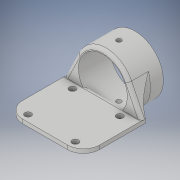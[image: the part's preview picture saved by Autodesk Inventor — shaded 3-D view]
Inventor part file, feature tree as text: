
AUTODESK INVENTOR PART (.ipt)
format: ipt  version: 2018 (Build 220112000, 112)  size: 258,048 bytes
history: native  units: in
note: dims shown in document units (in); Inventor stores cm internally (conversion verified against a paired STEP export)
features: extrude x7, sketch x5, fillet x5, plane x1
ambient origin geometry x8: Origin, YZ Plane, XZ Plane, XY Plane, X Axis, Y Axis, Z Axis, Center Point
bodies: Solid1 (feature_tree)
feature tree (18):
  sketch  "Sketch1"  dims[d0=1.2008in d1=0.0984in]
  extrude  "Extrusion1"  Depth=0.0984in
  plane  "Work Plane1"
  extrude  "Extrusion3"  Depth=1.8898in
  extrude  "Extrusion4"  Depth=0.0984in TaperAngle=0.0deg
  extrude  "Extrusion5"  Depth=1.4173in
  fillet  "Fillet2"  Radius=1.1614in
  extrude  "Extrusion6"  Depth=0.3937in
  fillet  "Fillet3"  Radius=0.1575in
  fillet  "Fillet5"  Radius=0.1575in
  fillet  "Fillet6"  Radius=0.1575in
  fillet  "Fillet7"  Radius=0.0984in
  extrude  "Extrusion7"  Depth=0.3937in TaperAngle=0.0deg
  extrude  "Extrusion8"  Depth=0.3937in
  sketch  "Sketch2"  dims[d2=1.1811in d3=0.0in d8=1.8898in]
  sketch  "Sketch3"  dims[d9=1.5157in d10=0.0984in d11=0.0in]
  sketch  "Sketch4"  dims[d12=1.8898in d13=1.4173in d14=1.1614in]
  sketch  "Sketch5"  dims[d15=1.0906in d16=0.1575in d17=0.1575in d18=0.1575in d19=0.1575in d20=0.0984in d21=0.0in d23=0.0984in d24=0.0in d25=0.3937in d26=0.0984in d27=0.0in d28=0.1181in d30=0.3937in d31=0.1181in d32=0.0787in d33=0.3937in d34=90.0deg d35=0.1181in d36=1.5748in d37=0.0in d38=0.3937in d39=0.0in]
